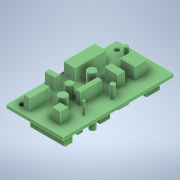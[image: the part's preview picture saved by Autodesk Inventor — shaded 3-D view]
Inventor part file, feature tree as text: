
AUTODESK INVENTOR PART (.ipt)
format: ipt  version: 2022 (Build 260153000, 153)  size: 239,616 bytes
history: native  units: mm
features: extrude x4, sketch x4
ambient origin geometry x8: Origin, YZ Plane, XZ Plane, XY Plane, X Axis, Y Axis, Z Axis, Center Point
bodies: Solid1 (feature_tree)
feature tree (8):
  extrude  "Extrusion1"  Depth=70.0mm
  extrude  "Extrusion2"  Depth=2.0mm
  extrude  "Extrusion3"  Depth=5.0mm
  extrude  "Extrusion4"  Depth=7.0mm
  sketch  "Sketch1"  dims[d0=36.0mm d1=70.0mm]
  sketch  "Sketch2"  dims[d2=2.0mm d3=0.0mm d4=3.0mm]
  sketch  "Sketch3"  dims[d5=3.0mm d6=5.0mm]
  sketch  "Sketch4"  dims[d9=0.0mm d10=0.0mm d11=60.0mm d12=5.0mm d13=8.0mm d14=0.0mm d15=7.0mm d16=0.0mm]
